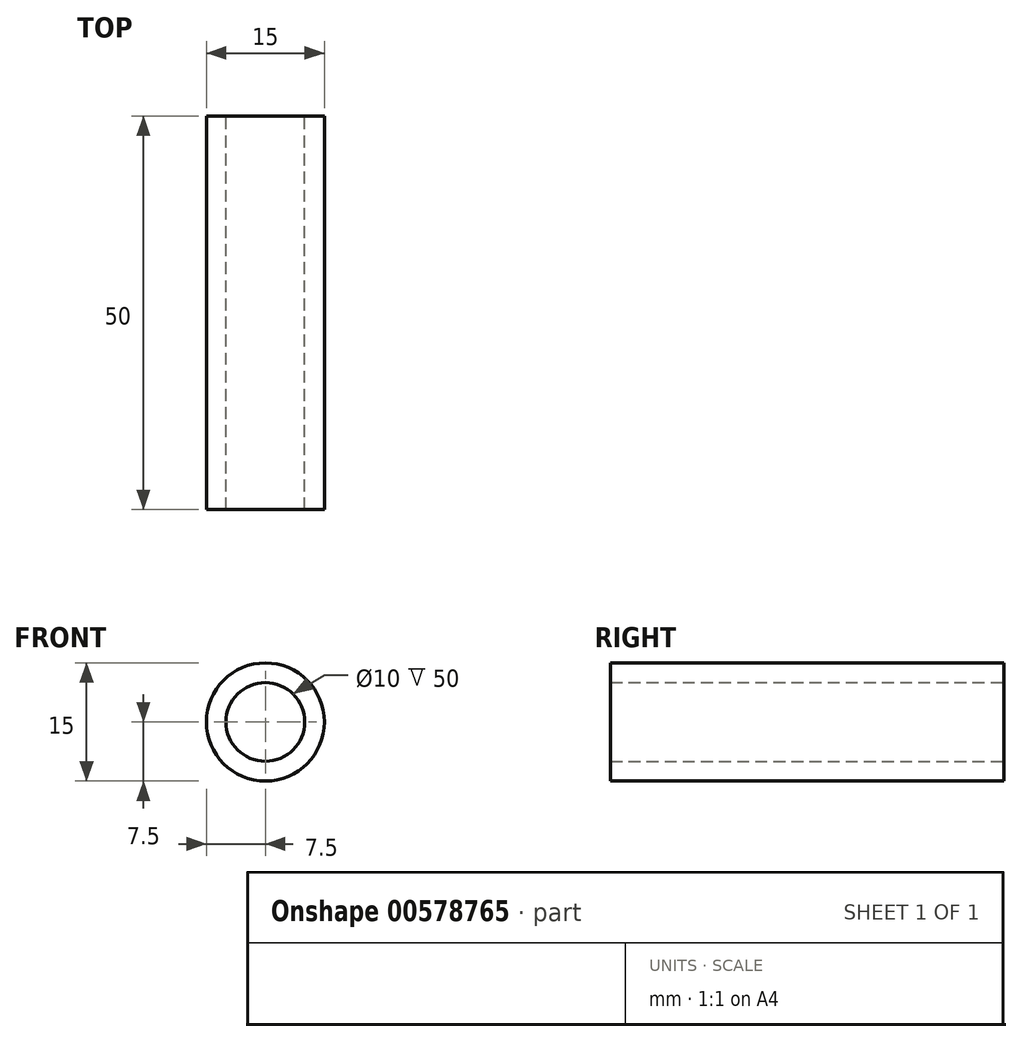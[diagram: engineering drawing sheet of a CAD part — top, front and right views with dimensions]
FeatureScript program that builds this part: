
annotation { "Feature Type Name" : "Feature", "Feature Type Description" : "" }
export const myFeature = defineFeature(function(context is Context, id is Id, definition is map)
    precondition{}
    {
        {
            var Q0;
            Q0=qCreatedBy(makeId("Front.planeOp"),FACE);
            var sketch = newSketch(context, id + "F0", { "sketchPlane" : qUnion([Q0])});
            skCircle(sketch, "E0", {"center": v(0, 0) * mm, "radius": 7.5 * mm});
            skCircle(sketch, "E1", {"center": v(0, 0) * mm, "radius": 5 * mm});
            skSolve(sketch);
        }
        {
            var Q0;
            Q0=qSketchRegion(id+"F0",true);
            extrude(context, id + "F1", {"entities" : qUnion([Q0]), "depth" : 50 * mm, "offsetDistance" : 25 * mm});
        }
    });
